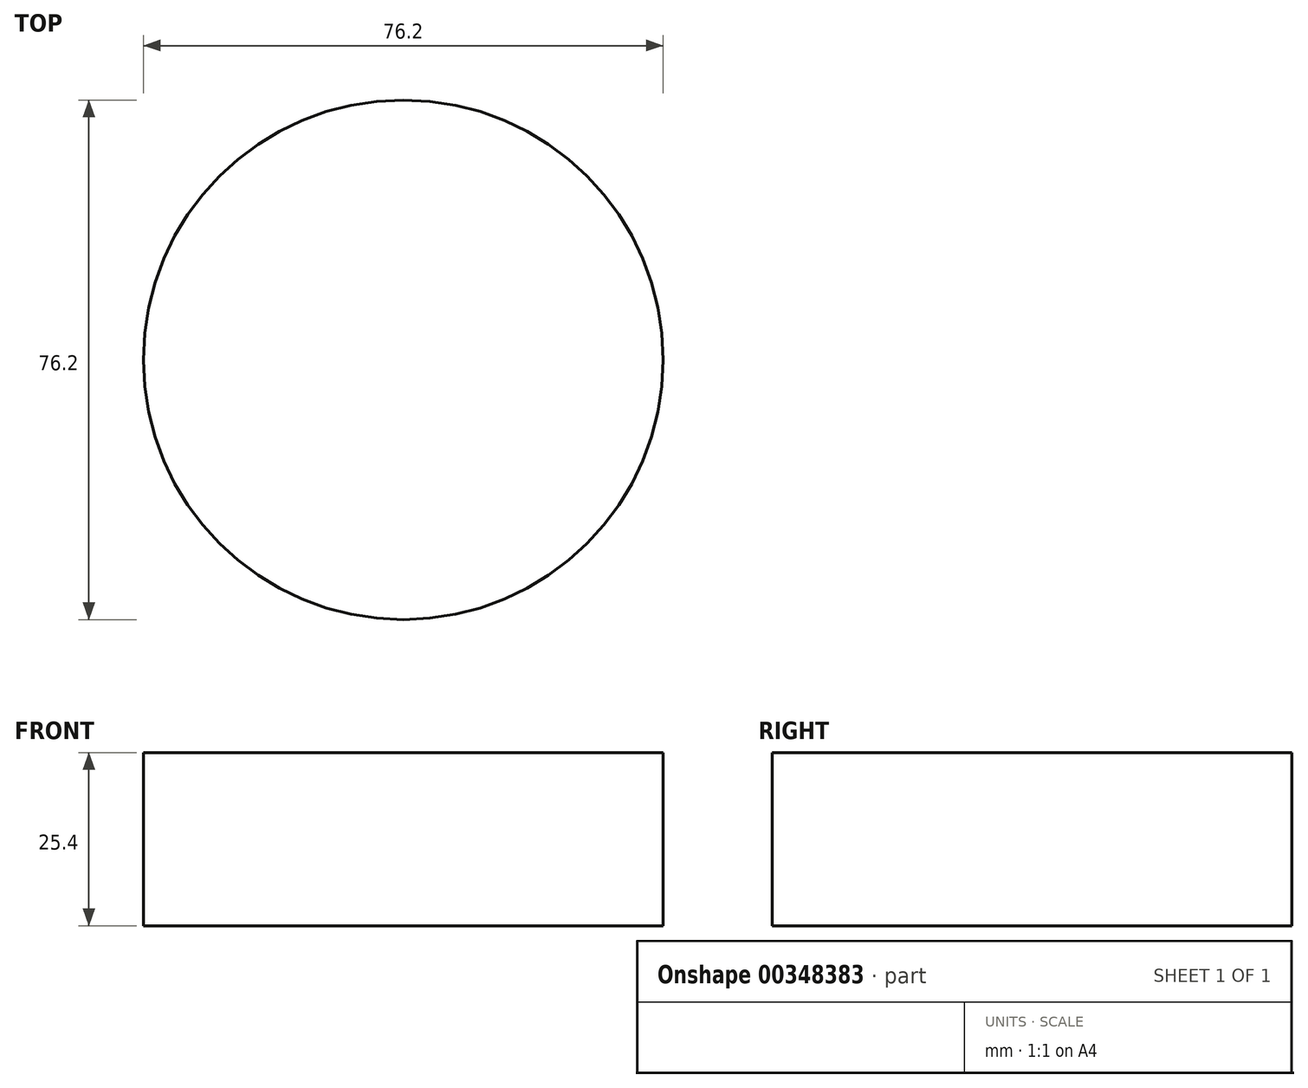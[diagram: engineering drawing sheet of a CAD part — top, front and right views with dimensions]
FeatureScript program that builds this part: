
annotation { "Feature Type Name" : "Feature", "Feature Type Description" : "" }
export const myFeature = defineFeature(function(context is Context, id is Id, definition is map)
    precondition{}
    {
        {
            var Q0;
            Q0=qCreatedBy(makeId("Top.planeOp"),FACE);
            var sketch = newSketch(context, id + "F0", { "sketchPlane" : qUnion([Q0])});
            skCircle(sketch, "E0", {"center": v(0, 0) * mm, "radius": 38.1 * mm});
            skSolve(sketch);
        }
        {
            var Q0;
            Q0=makeQuery(id+"F0.imprint","IMPRINT",FACE,{"disambiguationData":[TD([[makeQuery(id+"F0.imprint","IMPRINT",EDGE,{"derivedFrom":sQuery(id+"F0.wireOp",EDGE,"E0")}),1.0]])]});
            extrude(context, id + "F1", {"entities" : qUnion([Q0]), "endBound" : BoundingType.SYMMETRIC, "depth" : 25.4 * mm});
        }
    });
